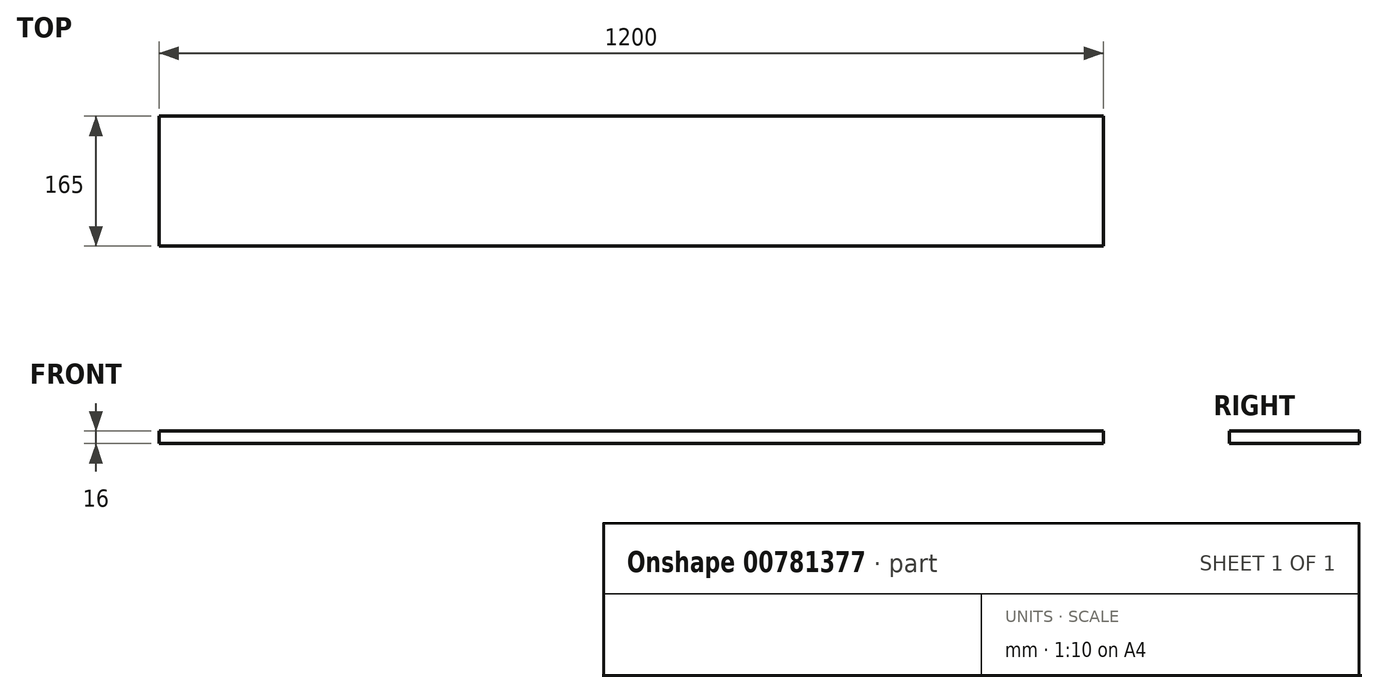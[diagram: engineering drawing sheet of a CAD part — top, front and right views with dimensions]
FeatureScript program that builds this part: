
annotation { "Feature Type Name" : "Feature", "Feature Type Description" : "" }
export const myFeature = defineFeature(function(context is Context, id is Id, definition is map)
    precondition{}
    {
        {
            var Q0;
            Q0=qCreatedBy(makeId("Top.planeOp"),FACE);
            var sketch = newSketch(context, id + "F0", { "sketchPlane" : qUnion([Q0])});
            skLineSegment(sketch, "E0.bottom", {"start": v(-600, -82.5) * mm, "end": v(600, -82.5) * mm});
            skLineSegment(sketch, "E0.top", {"start": v(-600, 82.5) * mm, "end": v(600, 82.5) * mm});
            skLineSegment(sketch, "E0.left", {"start": v(-600, -82.5) * mm, "end": v(-600, 82.5) * mm});
            skLineSegment(sketch, "E0.right", {"start": v(600, -82.5) * mm, "end": v(600, 82.5) * mm});
            skPoint(sketch, "E0.middle", {"position": v(0, 0) * mm});
            skSolve(sketch);
        }
        {
            var Q0;
            Q0 = qSketchRegion(id + "F0", true);
            extrude(context, id + "F1", {"entities" : qUnion([Q0]), "depth" : 16 * mm, "offsetDistance" : 25 * mm});
        }
    });
